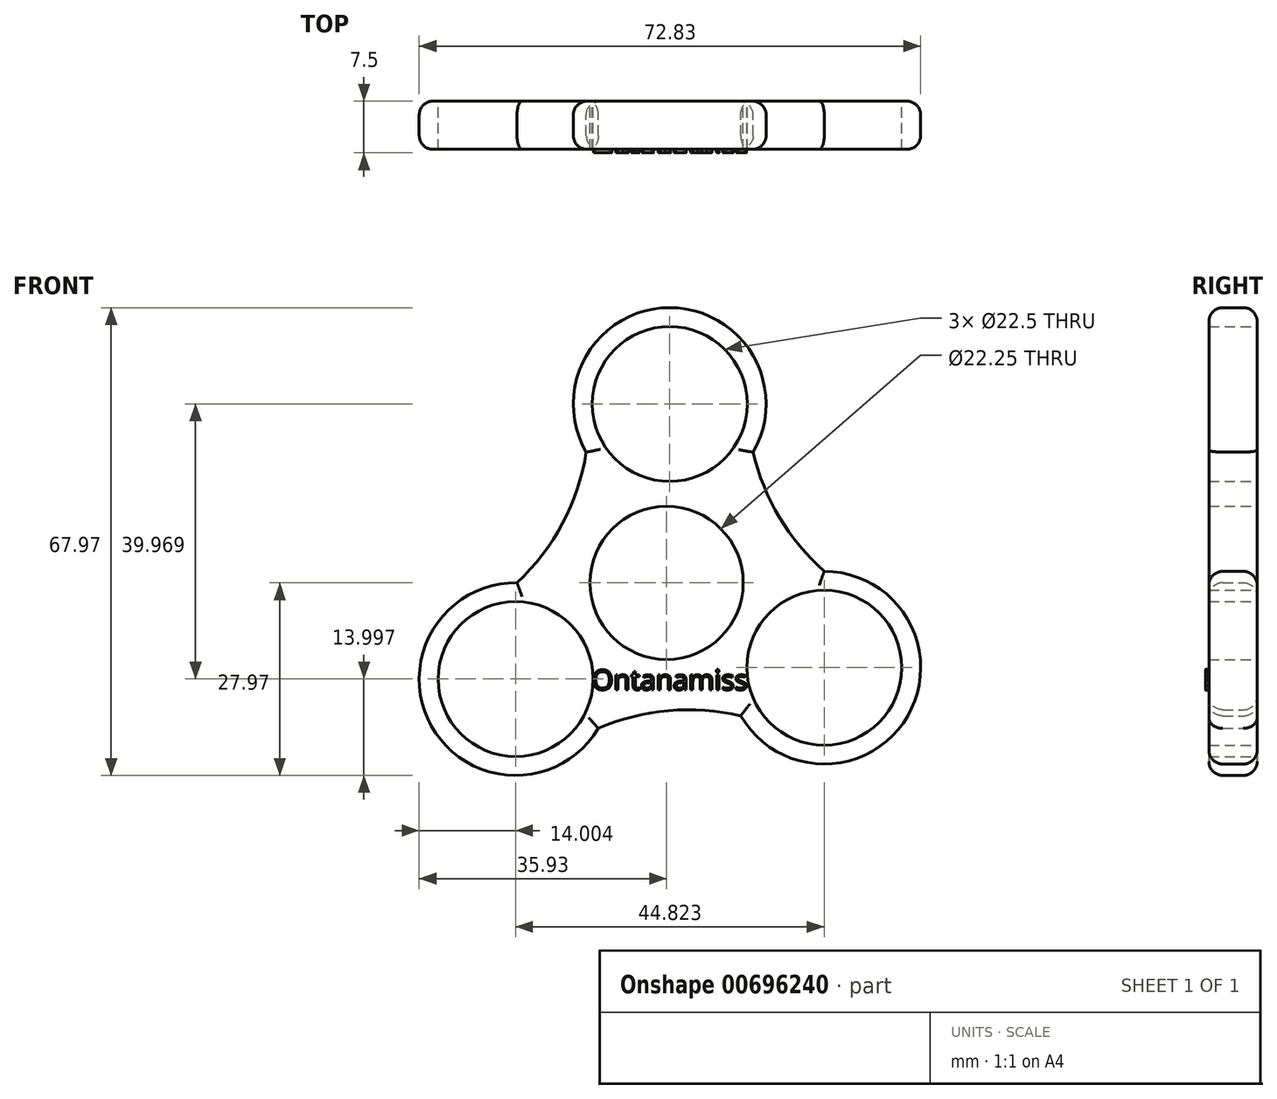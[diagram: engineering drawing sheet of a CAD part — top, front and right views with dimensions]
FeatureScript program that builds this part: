
annotation { "Feature Type Name" : "Feature", "Feature Type Description" : "" }
export const myFeature = defineFeature(function(context is Context, id is Id, definition is map)
    precondition{}
    {
        {
            var Q0;
            Q0=qCreatedBy(makeId("Front.planeOp"),FACE);
            var sketch = newSketch(context, id + "F0", { "sketchPlane" : qUnion([Q0])});
            skLineSegment(sketch, "E0", {"start": v(22.9, -12.32) * mm, "end": v(22.9, -12.32) * mm});
            skPoint(sketch, "E1.start.orphan", {"position": v(-21.65, 0) * mm});
            skPoint(sketch, "E2.end.orphan", {"position": v(22, 0) * mm});
            skCircle(sketch, "E3", {"center": v(0, 0) * mm, "radius": 11.12 * mm});
            skArc(sketch, "E4", {"start": v(12.58, 19) * mm, "mid": v(0.45, 40) * mm, "end": v(-11.67, 19) * mm});
            skArc(sketch, "E5", {"start": v(-21.73, 0.03) * mm, "mid": v(-34.15, -20.8) * mm, "end": v(-9.9, -21.15) * mm});
            skArc(sketch, "E6", {"start": v(10.77, -19.32) * mm, "mid": v(35.02, -19.32) * mm, "end": v(22.9, 1.68) * mm});
            skArc(sketch, "E7", {"start": v(-21.73, 0.03) * mm, "mid": v(-15.11, 8.67) * mm, "end": v(-11.67, 19) * mm});
            skArc(sketch, "E8", {"start": v(10.77, -19.32) * mm, "mid": v(0.29, -18.56) * mm, "end": v(-9.9, -21.15) * mm});
            skArc(sketch, "E9", {"start": v(12.58, 19) * mm, "mid": v(16.38, 9.53) * mm, "end": v(22.9, 1.68) * mm});
            skPoint(sketch, "E10.end.orphan", {"position": v(-21.65, 5.36) * mm});
            skCircle(sketch, "E11", {"center": v(-21.93, -13.97) * mm, "radius": 11.25 * mm});
            skCircle(sketch, "E12", {"center": v(22.9, -12.32) * mm, "radius": 11.25 * mm});
            skCircle(sketch, "E13", {"center": v(0.45, 26) * mm, "radius": 11.25 * mm});
            skSolve(sketch);
        }
        {
            var Q0;
            Q0 = qSketchRegion(id + "F0", true);
            extrude(context, id + "F1", {"entities" : qUnion([Q0]), "depth" : 7 * mm, "offsetDistance" : 25 * mm});
        }
        {
            var Q0;
            Q0=makeQuery(id+"F1.opExtrude","CAP_FACE",FACE,{"disambiguationData":[OSD([sQuery(id+"F0.wireOp",EDGE,"wDc6joGt-k8ni-1ecl-5bYh-xUhC9LoOSwOT"),sQuery(id+"F0.wireOp",EDGE,"ibCQJwPW-K3Z6-hY4c-BNDv-ag6xqu2csQdN"),sQuery(id+"F0.wireOp",EDGE,"B8quwXZ5-1ARu-7qBt-8SJ4-xmCsJpj4qHGd"),sQuery(id+"F0.wireOp",EDGE,"jLef8ziU-4658-4F8K-fGW8-hJX3s9XzRqc0"),sQuery(id+"F0.wireOp",EDGE,"ZfwbAWds-469a-XBV0-kuQN-TPMaF1y23ZnC"),sQuery(id+"F0.wireOp",EDGE,"mJ9T0A6Z-6Ad8-EKk2-63pD-fxuzAyV5lPIi"),sQuery(id+"F0.wireOp",EDGE,"9hDuoUn8-mQSL-roYn-ggjP-zJOSRf1HkW51"),sQuery(id+"F0.wireOp",EDGE,"KBa80Bsk-LTbe-RbyB-0Y7z-SaDBD6UvCs52"),sQuery(id+"F0.wireOp",EDGE,"FXuK8sul-GACR-RxKP-hkBe-b7t6UXiVBxcl"),sQuery(id+"F0.wireOp",EDGE,"E3")])],"isStart":false});
            var sketch = newSketch(context, id + "F2", { "sketchPlane" : qUnion([Q0])});
            skText(sketch, "E14", { "text": "Ontanamiss", "fontName": "OpenSans-Regular.ttf"});
            const initialGuessF2  = {"E14": [-0.01088, -0.01554, 1, 0, 0.00291]};
            skSetInitialGuess(sketch, initialGuessF2);
            skSolve(sketch);
        }
        {
            var Q0;
            Q0 = qSketchRegion(id + "F2", true);
            extrude(context, id + "F3", {"entities" : qUnion([Q0]), "operationType" : NewBodyOperationType.ADD, "depth" : .5 * mm, "offsetDistance" : 25 * mm});
        }
        {
            var Q0;
            Q0=makeQuery(id+"F1.opExtrude","CAP_EDGE",EDGE,{"disambiguationData":[OSD([sQuery(id+"F0.wireOp",EDGE,"E7")])],"isStart":false});
            var Q1;
            Q1=makeQuery(id+"F1.opExtrude","CAP_EDGE",EDGE,{"disambiguationData":[OSD([sQuery(id+"F0.wireOp",EDGE,"E5")])],"isStart":false});
            var Q2;
            Q2=makeQuery(id+"F1.opExtrude","CAP_EDGE",EDGE,{"disambiguationData":[OSD([sQuery(id+"F0.wireOp",EDGE,"E8")])],"isStart":false});
            var Q3;
            Q3=makeQuery(id+"F1.opExtrude","CAP_EDGE",EDGE,{"disambiguationData":[OSD([sQuery(id+"F0.wireOp",EDGE,"E6")])],"isStart":false});
            var Q4;
            Q4=makeQuery(id+"F1.opExtrude","CAP_EDGE",EDGE,{"disambiguationData":[OSD([sQuery(id+"F0.wireOp",EDGE,"E9")])],"isStart":false});
            var Q5;
            Q5=makeQuery(id+"F1.opExtrude","CAP_EDGE",EDGE,{"disambiguationData":[OSD([sQuery(id+"F0.wireOp",EDGE,"E4")])],"isStart":false});
            fillet(context, id + "F4", {"entities" : qUnion([Q0, Q1, Q2, Q3, Q4, Q5]), "radius" : 2 * mm, "tangentPropagation" : true, "allowEdgeOverflow" : false});
        }
        {
            var Q0;
            Q0=makeQuery(id+"F1.opExtrude","CAP_EDGE",EDGE,{"disambiguationData":[OSD([sQuery(id+"F0.wireOp",EDGE,"E6")])],"isStart":true});
            var Q1;
            Q1=makeQuery(id+"F1.opExtrude","CAP_EDGE",EDGE,{"disambiguationData":[OSD([sQuery(id+"F0.wireOp",EDGE,"E8")])],"isStart":true});
            var Q2;
            Q2=makeQuery(id+"F1.opExtrude","CAP_EDGE",EDGE,{"disambiguationData":[OSD([sQuery(id+"F0.wireOp",EDGE,"E9")])],"isStart":true});
            var Q3;
            Q3=makeQuery(id+"F1.opExtrude","CAP_EDGE",EDGE,{"disambiguationData":[OSD([sQuery(id+"F0.wireOp",EDGE,"E4")])],"isStart":true});
            var Q4;
            Q4=makeQuery(id+"F1.opExtrude","CAP_EDGE",EDGE,{"disambiguationData":[OSD([sQuery(id+"F0.wireOp",EDGE,"E7")])],"isStart":true});
            var Q5;
            Q5=makeQuery(id+"F1.opExtrude","CAP_EDGE",EDGE,{"disambiguationData":[OSD([sQuery(id+"F0.wireOp",EDGE,"E5")])],"isStart":true});
            fillet(context, id + "F5", {"entities" : qUnion([Q0, Q1, Q2, Q3, Q4, Q5]), "radius" : 2 * mm, "tangentPropagation" : true, "allowEdgeOverflow" : false});
        }
    });
